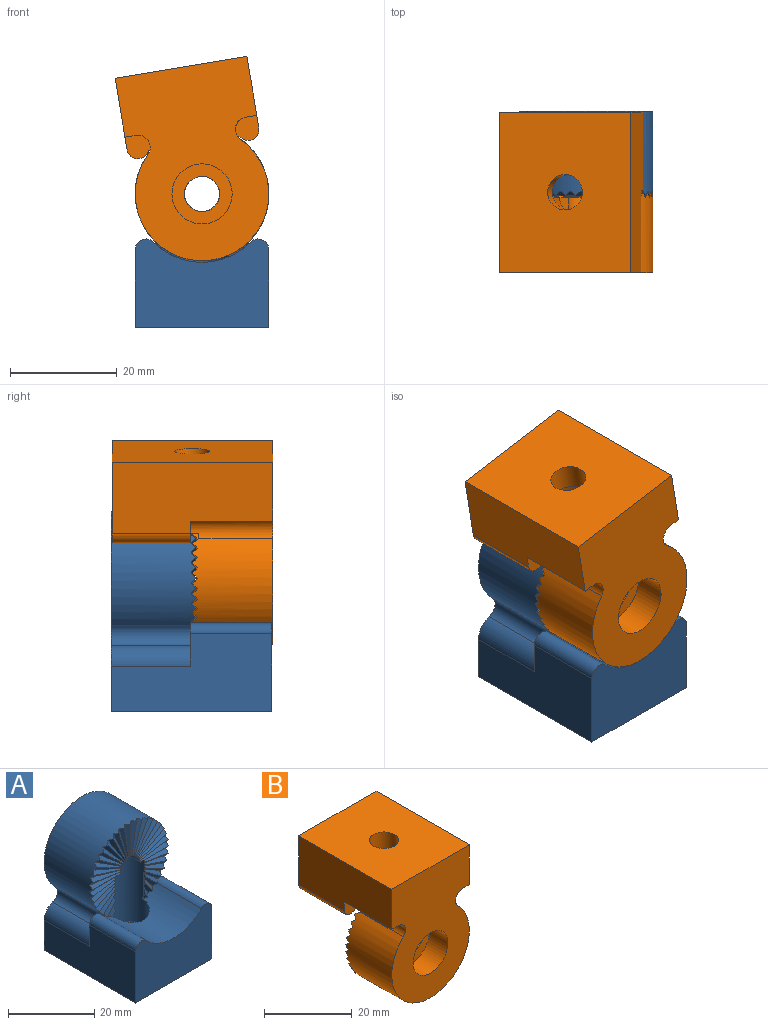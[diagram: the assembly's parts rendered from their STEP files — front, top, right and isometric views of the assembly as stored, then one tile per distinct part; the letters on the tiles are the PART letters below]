
ASSEMBLY  parts=2 mates=1
PART A: 135 faces, bbox 25.1x30.1x37.6 mm
  f0: plane 3.86x2.94mm, normal (0,-1,0), area 1.2mm2, adj f5,f6,f123,f130
  f1: plane 3.86x2.94mm, normal (0,-1,0), area 1.2mm2, adj f5,f6,f125,f130
  f2: cylinder r=3.3mm len=10.8mm, axis (0,1,0), area 169.4mm2, adj f8,f9,f10,f11,f12,f13,f16,f17
  f3: plane 7.62x0.85mm, normal (0,-0.73,-0.69), area 7mm2, adj f5,f42,f47,f91,f130
  f4: plane 7.62x0.85mm, normal (0,-0.73,-0.69), area 7mm2, adj f5,f39,f43,f92,f131
  f5: cylinder r=12.5mm len=25mm, axis (0,-1,0), area 910.5mm2, adj f0,f1,f3,f4,f7,f8,f9,f10
  f6: cylinder r=12.8mm len=18.16mm, axis (0,1,0), area 265.6mm2, adj f0,f1,f120,f121,f122,f124,f126,f130
  f7: plane 37.5x25mm, normal (0,1,0), area 727mm2, adj f5,f110,f111,f112,f113,f114,f115,f117
  f8: plane 9.21x0.85mm, normal (-0.69,-0.73,0), area 7.7mm2, adj f2,f5,f9,f11,f108
  f9: plane 9.21x0.85mm, normal (0.69,-0.73,0), area 7.7mm2, adj f2,f5,f8,f75,f109
  f10: plane 9.14x2.27mm, normal (-0.68,-0.73,-0.11), area 7.7mm2, adj f2,f5,f11,f12,f107
  f11: plane 9.19x1.7mm, normal (0.68,-0.73,0.11), area 7.7mm2, adj f2,f5,f8,f10,f108
  f12: plane 8.99x3.09mm, normal (0.65,-0.73,0.21), area 7.7mm2, adj f2,f5,f10,f13,f107
  f13: plane 8.84x3.64mm, normal (-0.65,-0.73,-0.21), area 7.7mm2, adj f2,f5,f12,f17,f106
  f14: plane 1.89x0.79mm, normal (-0.61,-0.73,-0.31), area 0.9mm2, adj f5,f15,f131
  f15: plane 3.06x1.53mm, normal (0.61,-0.73,0.31), area 2.8mm2, adj f5,f14,f21,f104,f131
  f16: plane 8.32x4.92mm, normal (-0.61,-0.73,-0.31), area 7.7mm2, adj f2,f5,f17,f18,f105
  f17: plane 8.56x4.41mm, normal (0.61,-0.73,0.31), area 7.7mm2, adj f2,f5,f13,f16,f106
  f18: plane 7.92x5.62mm, normal (0.55,-0.73,0.4), area 7.7mm2, adj f2,f5,f16,f19,f105
  f19: plane 7.6x6.08mm, normal (-0.55,-0.73,-0.4), area 7.7mm2, adj f2,f5,f18,f25,f103
  f20: plane 4.35x3.16mm, normal (0.55,-0.73,0.4), area 4.9mm2, adj f5,f21,f22,f102,f131
  f21: plane 3.9x2.49mm, normal (-0.55,-0.73,-0.4), area 4mm2, adj f5,f15,f20,f104,f131
  f22: plane 4.55x3.97mm, normal (-0.48,-0.73,-0.48), area 5.4mm2, adj f5,f20,f23,f102,f131
  f23: plane 4.63x4.55mm, normal (0.48,-0.73,0.48), area 5.9mm2, adj f5,f22,f29,f100,f131
  f24: plane 7.09x6.7mm, normal (-0.48,-0.73,-0.48), area 7.7mm2, adj f2,f5,f25,f26,f101
  f25: plane 7.09x6.7mm, normal (0.48,-0.73,0.48), area 7.7mm2, adj f2,f5,f19,f24,f103
  f26: plane 7.6x6.08mm, normal (0.4,-0.73,0.55), area 7.7mm2, adj f2,f5,f24,f27,f101
  f27: plane 7.92x5.62mm, normal (-0.4,-0.73,-0.55), area 7.7mm2, adj f2,f5,f26,f33,f99
  f28: plane 5.71x4.33mm, normal (0.4,-0.73,0.55), area 6.4mm2, adj f5,f29,f30,f98,f131
  f29: plane 5.23x4.48mm, normal (-0.4,-0.73,-0.55), area 6.2mm2, adj f5,f23,f28,f100,f131
  f30: plane 6.26x3.93mm, normal (-0.31,-0.73,-0.61), area 6.6mm2, adj f5,f28,f31,f98,f131
  f31: plane 6.62x3.64mm, normal (0.31,-0.73,0.61), area 6.7mm2, adj f5,f30,f37,f96,f131
  f32: plane 8.56x4.41mm, normal (-0.31,-0.73,-0.61), area 7.7mm2, adj f2,f5,f33,f34,f97
  f33: plane 8.32x4.92mm, normal (0.31,-0.73,0.61), area 7.7mm2, adj f2,f5,f27,f32,f99
  f34: plane 8.84x3.64mm, normal (0.21,-0.73,0.65), area 7.7mm2, adj f2,f5,f32,f35,f97
  f35: plane 8.99x3.09mm, normal (-0.21,-0.73,-0.65), area 7.7mm2, adj f2,f5,f34,f41,f95
  f36: plane 7.24x2.68mm, normal (0.21,-0.73,0.65), area 6.9mm2, adj f5,f37,f38,f94,f131
  f37: plane 7x3.08mm, normal (-0.21,-0.73,-0.65), area 6.8mm2, adj f5,f31,f36,f96,f131
  f38: plane 7.46x2.02mm, normal (-0.11,-0.73,-0.68), area 6.9mm2, adj f5,f36,f39,f94,f131
  f39: plane 7.57x1.57mm, normal (0.11,-0.73,0.68), area 7mm2, adj f4,f5,f38,f92,f131
  f40: plane 9.19x1.7mm, normal (-0.11,-0.73,-0.68), area 7.7mm2, adj f2,f5,f41,f42,f93
  f41: plane 9.14x2.27mm, normal (0.11,-0.73,0.68), area 7.7mm2, adj f2,f5,f35,f40,f95
  f42: plane 9.21x0.85mm, normal (0,-0.73,0.69), area 7.7mm2, adj f2,f3,f5,f40,f93,f127
  f43: plane 9.21x0.85mm, normal (0,-0.73,0.69), area 7.7mm2, adj f2,f4,f5,f44,f90,f132
  f44: plane 9.19x1.7mm, normal (0.11,-0.73,-0.68), area 7.7mm2, adj f2,f5,f43,f45,f90
  f45: plane 9.14x2.27mm, normal (-0.11,-0.73,0.68), area 7.7mm2, adj f2,f5,f44,f51,f88
  f46: plane 7.46x2.02mm, normal (0.11,-0.73,-0.68), area 6.9mm2, adj f5,f47,f48,f89,f130
  f47: plane 7.57x1.57mm, normal (-0.11,-0.73,0.68), area 7mm2, adj f3,f5,f46,f91,f130
  f48: plane 7.24x2.68mm, normal (-0.21,-0.73,0.65), area 6.9mm2, adj f5,f46,f49,f89,f130
  f49: plane 7x3.08mm, normal (0.21,-0.73,-0.65), area 6.8mm2, adj f5,f48,f55,f87,f130
  f50: plane 8.84x3.64mm, normal (-0.21,-0.73,0.65), area 7.7mm2, adj f2,f5,f51,f52,f86
  f51: plane 8.99x3.09mm, normal (0.21,-0.73,-0.65), area 7.7mm2, adj f2,f5,f45,f50,f88
  f52: plane 8.56x4.41mm, normal (0.31,-0.73,-0.61), area 7.7mm2, adj f2,f5,f50,f53,f86
  f53: plane 8.32x4.92mm, normal (-0.31,-0.73,0.61), area 7.7mm2, adj f2,f5,f52,f59,f84
  f54: plane 6.26x3.93mm, normal (0.31,-0.73,-0.61), area 6.6mm2, adj f5,f55,f56,f85,f130
  f55: plane 6.62x3.64mm, normal (-0.31,-0.73,0.61), area 6.7mm2, adj f5,f49,f54,f87,f130
  f56: plane 5.71x4.33mm, normal (-0.4,-0.73,0.55), area 6.4mm2, adj f5,f54,f57,f85,f130
  f57: plane 5.23x4.48mm, normal (0.4,-0.73,-0.55), area 6.2mm2, adj f5,f56,f63,f83,f130
  f58: plane 7.6x6.08mm, normal (-0.4,-0.73,0.55), area 7.7mm2, adj f2,f5,f59,f60,f82
  f59: plane 7.92x5.62mm, normal (0.4,-0.73,-0.55), area 7.7mm2, adj f2,f5,f53,f58,f84
  f60: plane 7.09x6.7mm, normal (0.48,-0.73,-0.48), area 7.7mm2, adj f2,f5,f58,f61,f82
  f61: plane 7.09x6.7mm, normal (-0.48,-0.73,0.48), area 7.7mm2, adj f2,f5,f60,f67,f80
  f62: plane 4.55x3.97mm, normal (0.48,-0.73,-0.48), area 5.4mm2, adj f5,f63,f64,f81,f130
  f63: plane 4.63x4.55mm, normal (-0.48,-0.73,0.48), area 5.9mm2, adj f5,f57,f62,f83,f130
  f64: plane 4.35x3.16mm, normal (-0.55,-0.73,0.4), area 4.9mm2, adj f5,f62,f65,f81,f130
  f65: plane 3.9x2.49mm, normal (0.55,-0.73,-0.4), area 4mm2, adj f5,f64,f71,f79,f130
  f66: plane 7.92x5.62mm, normal (-0.55,-0.73,0.4), area 7.7mm2, adj f2,f5,f67,f68,f78
  f67: plane 7.6x6.08mm, normal (0.55,-0.73,-0.4), area 7.7mm2, adj f2,f5,f61,f66,f80
  f68: plane 8.32x4.92mm, normal (0.61,-0.73,-0.31), area 7.7mm2, adj f2,f5,f66,f69,f78
  f69: plane 8.56x4.41mm, normal (-0.61,-0.73,0.31), area 7.7mm2, adj f2,f5,f68,f73,f77
  f70: plane 1.94x0.84mm, normal (0.61,-0.73,-0.31), area 0.9mm2, adj f5,f71,f130
  f71: plane 3.12x1.59mm, normal (-0.61,-0.73,0.31), area 2.8mm2, adj f5,f65,f70,f79,f130
  f72: plane 8.99x3.09mm, normal (-0.65,-0.73,0.21), area 7.7mm2, adj f2,f5,f73,f74,f76
  f73: plane 8.84x3.64mm, normal (0.65,-0.73,-0.21), area 7.7mm2, adj f2,f5,f69,f72,f77
  f74: plane 9.14x2.27mm, normal (0.68,-0.73,-0.11), area 7.7mm2, adj f2,f5,f72,f75,f76
  f75: plane 9.19x1.7mm, normal (-0.68,-0.73,0.11), area 7.7mm2, adj f2,f5,f9,f74,f109
  f76: plane 1.65x0.52mm, normal (0,-1,0), area 0.2mm2, adj f5,f72,f74
  f77: plane 1.59x0.76mm, normal (0,-1,0), area 0.2mm2, adj f5,f69,f73
  f78: plane 1.49x0.98mm, normal (0,-1,0), area 0.2mm2, adj f5,f66,f68
  f79: plane 1.49x0.98mm, normal (0,-1,0), area 0.2mm2, adj f5,f65,f71
  f80: plane 1.35x1.18mm, normal (0,-1,0), area 0.2mm2, adj f5,f61,f67
  f81: plane 1.35x1.18mm, normal (0,-1,0), area 0.2mm2, adj f5,f62,f64
  f82: plane 1.35x1.18mm, normal (0,-1,0), area 0.2mm2, adj f5,f58,f60
  f83: plane 1.35x1.18mm, normal (0,-1,0), area 0.2mm2, adj f5,f57,f63
  f84: plane 1.49x0.98mm, normal (0,-1,0), area 0.2mm2, adj f5,f53,f59
  f85: plane 1.49x0.98mm, normal (0,-1,0), area 0.2mm2, adj f5,f54,f56
  f86: plane 1.59x0.76mm, normal (0,-1,0), area 0.2mm2, adj f5,f50,f52
  f87: plane 1.59x0.76mm, normal (0,-1,0), area 0.2mm2, adj f5,f49,f55
  f88: plane 1.65x0.52mm, normal (0,-1,0), area 0.2mm2, adj f5,f45,f51
  f89: plane 1.65x0.52mm, normal (0,-1,0), area 0.2mm2, adj f5,f46,f48
  f90: plane 1.67x0.26mm, normal (0,-1,0), area 0.2mm2, adj f5,f43,f44
  f91: plane 1.67x0.26mm, normal (0,-1,0), area 0.2mm2, adj f3,f5,f47
  f92: plane 1.67x0.26mm, normal (0,-1,0), area 0.2mm2, adj f4,f5,f39
  f93: plane 1.67x0.26mm, normal (0,-1,0), area 0.2mm2, adj f5,f40,f42
  f94: plane 1.65x0.52mm, normal (0,-1,0), area 0.2mm2, adj f5,f36,f38
  f95: plane 1.65x0.52mm, normal (0,-1,0), area 0.2mm2, adj f5,f35,f41
  f96: plane 1.59x0.76mm, normal (0,-1,0), area 0.2mm2, adj f5,f31,f37
  f97: plane 1.59x0.76mm, normal (0,-1,0), area 0.2mm2, adj f5,f32,f34
  f98: plane 1.49x0.98mm, normal (0,-1,0), area 0.2mm2, adj f5,f28,f30
  f99: plane 1.49x0.98mm, normal (0,-1,0), area 0.2mm2, adj f5,f27,f33
  f100: plane 1.35x1.18mm, normal (0,-1,0), area 0.2mm2, adj f5,f23,f29
  f101: plane 1.35x1.18mm, normal (0,-1,0), area 0.2mm2, adj f5,f24,f26
  f102: plane 1.35x1.18mm, normal (0,-1,0), area 0.2mm2, adj f5,f20,f22
  f103: plane 1.35x1.18mm, normal (0,-1,0), area 0.2mm2, adj f5,f19,f25
  f104: plane 1.49x0.98mm, normal (0,-1,0), area 0.2mm2, adj f5,f15,f21
  f105: plane 1.49x0.98mm, normal (0,-1,0), area 0.2mm2, adj f5,f16,f18
  f106: plane 1.59x0.76mm, normal (0,-1,0), area 0.2mm2, adj f5,f13,f17
  f107: plane 1.65x0.52mm, normal (0,-1,0), area 0.2mm2, adj f5,f10,f12
  f108: plane 1.67x0.26mm, normal (0,-1,0), area 0.2mm2, adj f5,f8,f11
  f109: plane 1.67x0.26mm, normal (0,-1,0), area 0.2mm2, adj f5,f9,f75
  f110: plane 5x5mm, normal (0.5,0,-0.87), area 28.9mm2, adj f7,f111,f115,f116
  f111: plane 5x5mm, normal (-0.5,0,-0.87), area 28.9mm2, adj f7,f110,f112,f116
  f112: plane 5.77x5mm, normal (-1,0,0), area 28.9mm2, adj f7,f111,f113,f116
  f113: plane 5x5mm, normal (-0.5,0,0.87), area 28.9mm2, adj f7,f112,f114,f116
  f114: plane 5x5mm, normal (0.5,0,0.87), area 28.9mm2, adj f7,f113,f115,f116
  f115: plane 5.77x5mm, normal (1,0,0), area 28.9mm2, adj f7,f110,f114,f116
  f116: plane 11.55x10mm, normal (0,1,0), area 52.4mm2, adj f2,f110,f111,f112,f113,f114,f115
  f117: plane 30x14.57mm, normal (-1,0,0), area 347.3mm2, adj f7,f119,f120,f122,f124,f134
  f118: plane 30x14.57mm, normal (1,0,0), area 347.3mm2, adj f7,f119,f120,f121,f126,f133
  f119: plane 30x25mm, normal (0,0,-1), area 715.8mm2, adj f7,f117,f118,f120,f128
  f120: plane 25x16.57mm, normal (0,-1,0), area 354mm2, adj f6,f117,f118,f119,f121,f122
  f121: cylinder r=2mm len=15.2mm, axis (0,1,0), area 71.7mm2, adj f6,f118,f120,f126
  f122: cylinder r=2mm len=15.2mm, axis (0,1,0), area 71.7mm2, adj f6,f117,f120,f124
  f123: cylinder r=2.3mm len=14.8mm, axis (0,1,0), area 69.7mm2, adj f0,f5,f7,f124,f134
  f124: plane 8.07x4.37mm, normal (0,1,0), area 18.4mm2, adj f6,f117,f122,f123,f134
  f125: cylinder r=2.3mm len=14.8mm, axis (0,1,0), area 69.7mm2, adj f1,f5,f7,f126,f133
  f126: plane 8.07x4.37mm, normal (0,1,0), area 18.4mm2, adj f6,f118,f121,f125,f133
  f127: plane 4.49x1.65mm, normal (0,0,-1), area 5.5mm2, adj f2,f42,f130
  f128: cylinder r=3.3mm len=6.6mm, axis (0,0,1), area 124.4mm2, adj f119,f129
  f129: plane 9.9x9.9mm, normal (0,0,1), area 42.8mm2, adj f128,f130
  f130: cylinder r=4.95mm len=19mm, axis (0,0,1), area 387.1mm2, adj f0,f1,f2,f3,f5,f6,f46,f47
  f131: cylinder r=4.95mm len=11.48mm, axis (0,0,1), area 6mm2, adj f4,f5,f14,f15,f20,f21,f22,f23
  f132: plane 4.49x1.65mm, normal (0,0,-1), area 5.5mm2, adj f2,f43,f130,f131
  f133: cylinder r=4mm len=14.8mm, axis (0,1,0), area 74.6mm2, adj f7,f118,f125,f126
  f134: cylinder r=4mm len=14.8mm, axis (0,1,0), area 74.6mm2, adj f7,f117,f123,f124
PART B: 142 faces, bbox 25.1x30.1x36.6 mm
  f0: plane 25x15.57mm, normal (0,1,0), area 275.7mm2, adj f3,f8,f9,f81,f82,f83,f95,f96
  f1: plane 3.67x2.84mm, normal (0,1,0), area 1.2mm2, adj f3,f4,f84,f91
  f2: plane 3.67x2.84mm, normal (0,1,0), area 1.2mm2, adj f3,f4,f87,f91
  f3: cylinder r=12.8mm len=18.16mm, axis (0,-1,0), area 266.2mm2, adj f0,f1,f2,f8,f9,f84,f85,f87
  f4: cylinder r=12.5mm len=25mm, axis (0,1,0), area 861.6mm2, adj f1,f2,f6,f7,f10,f11,f12,f15
  f5: cylinder r=3.3mm len=8.26mm, axis (0,-1,0), area 129mm2, adj f10,f12,f13,f15,f16,f17,f18,f21
  f6: plane 7.35x0.98mm, normal (0,0.71,-0.71), area 7.2mm2, adj f4,f47,f51,f91
  f7: plane 7.35x0.98mm, normal (0,0.71,-0.71), area 7.2mm2, adj f4,f44,f48,f91
  f8: cylinder r=2mm len=14.6mm, axis (0,-1,0), area 68.9mm2, adj f0,f3,f81,f88
  f9: cylinder r=2mm len=14.6mm, axis (0,-1,0), area 68.9mm2, adj f0,f3,f83,f85
  f10: plane 9.21x0.98mm, normal (0.71,0.71,0), area 8.1mm2, adj f4,f5,f12,f16
  f11: plane 36.5x25mm, normal (0,-1,0), area 693.8mm2, adj f4,f14,f81,f82,f83,f84,f86,f87
  f12: plane 9.21x0.98mm, normal (-0.71,0.71,0), area 8.1mm2, adj f4,f5,f10,f80
  f13: plane 11.25x11.25mm, normal (0,-1,0), area 65.2mm2, adj f5,f14
  f14: cylinder r=5.62mm len=11.25mm, axis (0,-1,0), area 212.1mm2, adj f11,f13
  f15: plane 9.14x2.4mm, normal (0.7,0.71,-0.11), area 8.1mm2, adj f4,f5,f16,f17
  f16: plane 9.2x1.7mm, normal (-0.7,0.71,0.11), area 8.1mm2, adj f4,f5,f10,f15
  f17: plane 9.02x3.09mm, normal (-0.67,0.71,0.22), area 8.1mm2, adj f4,f5,f15,f18
  f18: plane 8.84x3.76mm, normal (0.67,0.71,-0.22), area 8.1mm2, adj f4,f5,f17,f21
  f19: plane 1.26x0.54mm, normal (0.63,0.71,-0.32), area 0.4mm2, adj f4,f20,f91
  f20: plane 2.64x1.44mm, normal (-0.63,0.71,0.32), area 2.3mm2, adj f4,f19,f25,f91
  f21: plane 8.61x4.41mm, normal (-0.63,0.71,0.32), area 8.1mm2, adj f4,f5,f18,f22
  f22: plane 8.32x5.03mm, normal (0.63,0.71,-0.32), area 8.1mm2, adj f4,f5,f21,f23
  f23: plane 7.99x5.62mm, normal (-0.57,0.71,0.42), area 8.1mm2, adj f4,f5,f22,f24
  f24: plane 7.6x6.18mm, normal (0.57,0.71,-0.42), area 8.1mm2, adj f4,f5,f23,f29
  f25: plane 3.6x2.23mm, normal (0.57,0.71,-0.42), area 3.8mm2, adj f4,f20,f26,f91
  f26: plane 4.01x3mm, normal (-0.57,0.71,0.42), area 4.7mm2, adj f4,f25,f27,f91
  f27: plane 4.37x3.7mm, normal (0.5,0.71,-0.5), area 5.4mm2, adj f4,f26,f28,f91
  f28: plane 4.39x4.37mm, normal (-0.5,0.71,0.5), area 5.9mm2, adj f4,f27,f33,f91
  f29: plane 7.17x6.7mm, normal (-0.5,0.71,0.5), area 8.1mm2, adj f4,f5,f24,f30
  f30: plane 7.17x6.7mm, normal (0.5,0.71,-0.5), area 8.1mm2, adj f4,f5,f29,f31
  f31: plane 7.6x6.18mm, normal (-0.42,0.71,0.57), area 8.1mm2, adj f4,f5,f30,f32
  f32: plane 7.99x5.62mm, normal (0.42,0.71,-0.57), area 8.1mm2, adj f4,f5,f31,f37
  f33: plane 4.97x4.38mm, normal (0.42,0.71,-0.57), area 6.2mm2, adj f4,f28,f34,f91
  f34: plane 5.51x4.16mm, normal (-0.42,0.71,0.57), area 6.5mm2, adj f4,f33,f35,f91
  f35: plane 5.99x3.91mm, normal (0.32,0.71,-0.63), area 6.7mm2, adj f4,f34,f36,f91
  f36: plane 6.4x3.52mm, normal (-0.32,0.71,0.63), area 6.9mm2, adj f4,f35,f41,f91
  f37: plane 8.32x5.03mm, normal (-0.32,0.71,0.63), area 8.1mm2, adj f4,f5,f32,f38
  f38: plane 8.61x4.41mm, normal (0.32,0.71,-0.63), area 8.1mm2, adj f4,f5,f37,f39
  f39: plane 8.84x3.76mm, normal (-0.22,0.71,0.67), area 8.1mm2, adj f4,f5,f38,f40
  f40: plane 9.02x3.09mm, normal (0.22,0.71,-0.67), area 8.1mm2, adj f4,f5,f39,f45
  f41: plane 6.74x3.11mm, normal (0.22,0.71,-0.67), area 7mm2, adj f4,f36,f42,f91
  f42: plane 7x2.61mm, normal (-0.22,0.71,0.67), area 7.1mm2, adj f4,f41,f43,f91
  f43: plane 7.19x2.1mm, normal (0.11,0.71,-0.7), area 7.1mm2, adj f4,f42,f44,f91
  f44: plane 7.31x1.55mm, normal (-0.11,0.71,0.7), area 7.2mm2, adj f4,f7,f43,f91
  f45: plane 9.14x2.4mm, normal (-0.11,0.71,0.7), area 8.1mm2, adj f4,f5,f40,f46
  f46: plane 9.2x1.7mm, normal (0.11,0.71,-0.7), area 8.1mm2, adj f4,f5,f45,f47
  f47: plane 9.21x0.98mm, normal (0,0.71,0.71), area 8.1mm2, adj f4,f5,f6,f46,f90
  f48: plane 9.21x0.98mm, normal (0,0.71,0.71), area 8.1mm2, adj f4,f5,f7,f49,f94
  f49: plane 9.2x1.7mm, normal (-0.11,0.71,-0.7), area 8.1mm2, adj f4,f5,f48,f50
  f50: plane 9.14x2.4mm, normal (0.11,0.71,0.7), area 8.1mm2, adj f4,f5,f49,f55
  f51: plane 7.31x1.55mm, normal (0.11,0.71,0.7), area 7.2mm2, adj f4,f6,f52,f91
  f52: plane 7.19x2.1mm, normal (-0.11,0.71,-0.7), area 7.1mm2, adj f4,f51,f53,f91
  f53: plane 7x2.61mm, normal (0.22,0.71,0.67), area 7.1mm2, adj f4,f52,f54,f91
  f54: plane 6.74x3.11mm, normal (-0.22,0.71,-0.67), area 7mm2, adj f4,f53,f59,f91
  f55: plane 9.02x3.09mm, normal (-0.22,0.71,-0.67), area 8.1mm2, adj f4,f5,f50,f56
  f56: plane 8.84x3.76mm, normal (0.22,0.71,0.67), area 8.1mm2, adj f4,f5,f55,f57
  f57: plane 8.61x4.41mm, normal (-0.32,0.71,-0.63), area 8.1mm2, adj f4,f5,f56,f58
  f58: plane 8.32x5.03mm, normal (0.32,0.71,0.63), area 8.1mm2, adj f4,f5,f57,f63
  f59: plane 6.4x3.52mm, normal (0.32,0.71,0.63), area 6.9mm2, adj f4,f54,f60,f91
  f60: plane 5.99x3.91mm, normal (-0.32,0.71,-0.63), area 6.7mm2, adj f4,f59,f61,f91
  f61: plane 5.51x4.16mm, normal (0.42,0.71,0.57), area 6.5mm2, adj f4,f60,f62,f91
  f62: plane 4.97x4.38mm, normal (-0.42,0.71,-0.57), area 6.2mm2, adj f4,f61,f67,f91
  f63: plane 7.99x5.62mm, normal (-0.42,0.71,-0.57), area 8.1mm2, adj f4,f5,f58,f64
  f64: plane 7.6x6.18mm, normal (0.42,0.71,0.57), area 8.1mm2, adj f4,f5,f63,f65
  f65: plane 7.17x6.7mm, normal (-0.5,0.71,-0.5), area 8.1mm2, adj f4,f5,f64,f66
  f66: plane 7.17x6.7mm, normal (0.5,0.71,0.5), area 8.1mm2, adj f4,f5,f65,f71
  f67: plane 4.39x4.37mm, normal (0.5,0.71,0.5), area 5.9mm2, adj f4,f62,f68,f91
  f68: plane 4.37x3.7mm, normal (-0.5,0.71,-0.5), area 5.4mm2, adj f4,f67,f69,f91
  f69: plane 4.01x3mm, normal (0.57,0.71,0.42), area 4.7mm2, adj f4,f68,f70,f91
  f70: plane 3.6x2.23mm, normal (-0.57,0.71,-0.42), area 3.8mm2, adj f4,f69,f75,f91
  f71: plane 7.6x6.18mm, normal (-0.57,0.71,-0.42), area 8.1mm2, adj f4,f5,f66,f72
  f72: plane 7.99x5.62mm, normal (0.57,0.71,0.42), area 8.1mm2, adj f4,f5,f71,f73
  f73: plane 8.32x5.03mm, normal (-0.63,0.71,-0.32), area 8.1mm2, adj f4,f5,f72,f74
  f74: plane 8.61x4.41mm, normal (0.63,0.71,0.32), area 8.1mm2, adj f4,f5,f73,f77
  f75: plane 2.64x1.44mm, normal (0.63,0.71,0.32), area 2.3mm2, adj f4,f70,f76,f91
  f76: plane 1.26x0.54mm, normal (-0.63,0.71,-0.32), area 0.4mm2, adj f4,f75,f91
  f77: plane 8.84x3.76mm, normal (-0.67,0.71,-0.22), area 8.1mm2, adj f4,f5,f74,f78
  f78: plane 9.02x3.09mm, normal (0.67,0.71,0.22), area 8.1mm2, adj f4,f5,f77,f79
  f79: plane 9.14x2.4mm, normal (-0.7,0.71,-0.11), area 8.1mm2, adj f4,f5,f78,f80
  f80: plane 9.2x1.7mm, normal (0.7,0.71,0.11), area 8.1mm2, adj f4,f5,f12,f79
  f81: plane 30x13.57mm, normal (1,0,0), area 370mm2, adj f0,f8,f11,f82,f88,f89
  f82: plane 30x25mm, normal (0,0,1), area 715.8mm2, adj f0,f11,f81,f83,f92
  f83: plane 30x13.57mm, normal (-1,0,0), area 370mm2, adj f0,f9,f11,f82,f85,f86
  f84: cylinder r=2.3mm len=15.4mm, axis (0,-1,0), area 81.8mm2, adj f1,f3,f4,f11,f85,f86
  f85: plane 4.41x4.4mm, normal (0,-1,0), area 16.1mm2, adj f3,f9,f83,f84,f86
  f86: plane 15.4x2.11mm, normal (0,0,-1), area 32.4mm2, adj f11,f83,f84,f85
  f87: cylinder r=2.3mm len=15.4mm, axis (0,-1,0), area 81.8mm2, adj f2,f3,f4,f11,f88,f89
  f88: plane 4.41x4.4mm, normal (0,-1,0), area 16.1mm2, adj f3,f8,f81,f87,f89
  f89: plane 15.4x2.11mm, normal (0,0,-1), area 32.4mm2, adj f11,f81,f87,f88
  f90: plane 3.08x1.85mm, normal (0,0,1), area 3.6mm2, adj f5,f47,f91
  f91: cylinder r=5.25mm len=19mm, axis (0,0,-1), area 389.8mm2, adj f1,f2,f3,f4,f5,f6,f7,f19
  f92: cylinder r=3.3mm len=6.6mm, axis (0,0,-1), area 103.7mm2, adj f82,f93
  f93: plane 10.5x10.5mm, normal (0,0,-1), area 52.4mm2, adj f91,f92
  f94: plane 3.08x1.85mm, normal (0,0,1), area 3.6mm2, adj f5,f48,f91
  f95: extruded ~1.59x1mm, area 1.6mm2, adj f0,f96,f119,f120
  f96: extruded ~1x1mm, area 1.3mm2, adj f0,f95,f97,f120
  f97: extruded ~1.29x1mm, area 1.4mm2, adj f0,f96,f98,f120
  f98: extruded ~1.67x1mm, area 1.8mm2, adj f0,f97,f99,f120
  f99: extruded ~1.69x1mm, area 1.8mm2, adj f0,f98,f100,f120
  f100: extruded ~1.55x1mm, area 1.7mm2, adj f0,f99,f101,f120
  f101: extruded ~1.4x1mm, area 1.6mm2, adj f0,f100,f102,f120
  f102: extruded ~1.45x1mm, area 1.7mm2, adj f0,f101,f103,f120
  f103: plane 1x0.06mm, normal (0,0,-1), area 0.1mm2, adj f0,f102,f104,f120
  f104: extruded ~1.22x1mm, area 1.3mm2, adj f0,f103,f105,f120
  f105: extruded ~1x0.69mm, area 1mm2, adj f0,f104,f106,f120
  f106: extruded ~1.19x1mm, area 1.2mm2, adj f0,f105,f107,f120
  f107: extruded ~1x0.8mm, area 0.8mm2, adj f0,f106,f108,f120
  f108: plane 1.13x1mm, normal (1,0,0), area 1.1mm2, adj f0,f107,f109,f120
  f109: extruded ~1x0.9mm, area 0.9mm2, adj f0,f108,f110,f120
  f110: extruded ~2.51x1mm, area 2.8mm2, adj f0,f109,f119,f120
  f111: extruded ~1x0.72mm, area 0.8mm2, adj f112,f118,f120,f121
  f112: extruded ~1x0.92mm, area 1mm2, adj f111,f113,f120,f121
  f113: extruded ~1x0.65mm, area 0.7mm2, adj f112,f114,f120,f121
  f114: extruded ~1x0.73mm, area 0.8mm2, adj f113,f115,f120,f121
  f115: extruded ~1x0.68mm, area 0.8mm2, adj f114,f116,f120,f121
  f116: extruded ~1x0.77mm, area 0.8mm2, adj f115,f117,f120,f121
  f117: extruded ~1x0.87mm, area 0.9mm2, adj f116,f118,f120,f121
  f118: extruded ~1x0.69mm, area 0.8mm2, adj f111,f117,f120,f121
  f119: extruded ~2.95x1mm, area 3.1mm2, adj f0,f95,f110,f120
  f120: plane 6.85x4.72mm, normal (0,1,0), area 19mm2, adj f95,f96,f97,f98,f99,f100,f101,f102
  f121: plane 2.22x1.95mm, normal (0,1,0), area 3.5mm2, adj f111,f112,f113,f114,f115,f116,f117,f118
  f122: plane 1.3x1mm, normal (0,0,1), area 1.3mm2, adj f0,f123,f140,f141
  f123: plane 5.23x1.72mm, normal (0.95,0,0.31), area 5.5mm2, adj f0,f122,f124,f141
  f124: plane 1x0.04mm, normal (0,0,1), area 0mm2, adj f0,f123,f125,f141
  f125: extruded ~1.55x1mm, area 1.6mm2, adj f0,f124,f126,f141
  f126: extruded ~1x0.52mm, area 0.5mm2, adj f0,f125,f127,f141
  f127: plane 3.16x1mm, normal (-1,0,0), area 3.2mm2, adj f0,f126,f128,f141
  f128: plane 1.32x1mm, normal (0,0,1), area 1.3mm2, adj f0,f127,f129,f141
  f129: plane 6.68x1mm, normal (1,0,0), area 6.7mm2, adj f0,f128,f130,f141
  f130: plane 1.93x1mm, normal (0,0,-1), area 1.9mm2, adj f0,f129,f131,f141
  f131: plane 5.11x1.68mm, normal (-0.95,0,-0.31), area 5.4mm2, adj f0,f130,f132,f141
  f132: plane 1x0.03mm, normal (0,0,-1), area 0mm2, adj f0,f131,f133,f141
  f133: plane 5.11x1.58mm, normal (0.96,0,-0.3), area 5.3mm2, adj f0,f132,f134,f141
  f134: plane 1.93x1mm, normal (0,0,-1), area 1.9mm2, adj f0,f133,f135,f141
  f135: plane 6.68x1mm, normal (-1,0,0), area 6.7mm2, adj f0,f134,f136,f141
  f136: plane 1.27x1mm, normal (0,0,1), area 1.3mm2, adj f0,f135,f137,f141
  f137: plane 3.11x1mm, normal (1,0,0), area 3.1mm2, adj f0,f136,f138,f141
  f138: extruded ~2.13x1mm, area 2.1mm2, adj f0,f137,f139,f141
  f139: plane 1x0.04mm, normal (0,0,1), area 0mm2, adj f0,f138,f140,f141
  f140: plane 5.24x1.61mm, normal (-0.96,0,0.29), area 5.5mm2, adj f0,f122,f139,f141
  f141: plane 7.14x6.68mm, normal (0,1,0), area 30.8mm2, adj f122,f123,f124,f125,f126,f127,f128,f129
PLACE A at identity fixed
PLACE B rot(axis=(0,-1,0),9.4deg) t=(0,-0.17,0)mm
MATE revolute B.f3 <-> A.f2  axis (0,-1,0) through (0,-0.86,0)mm
